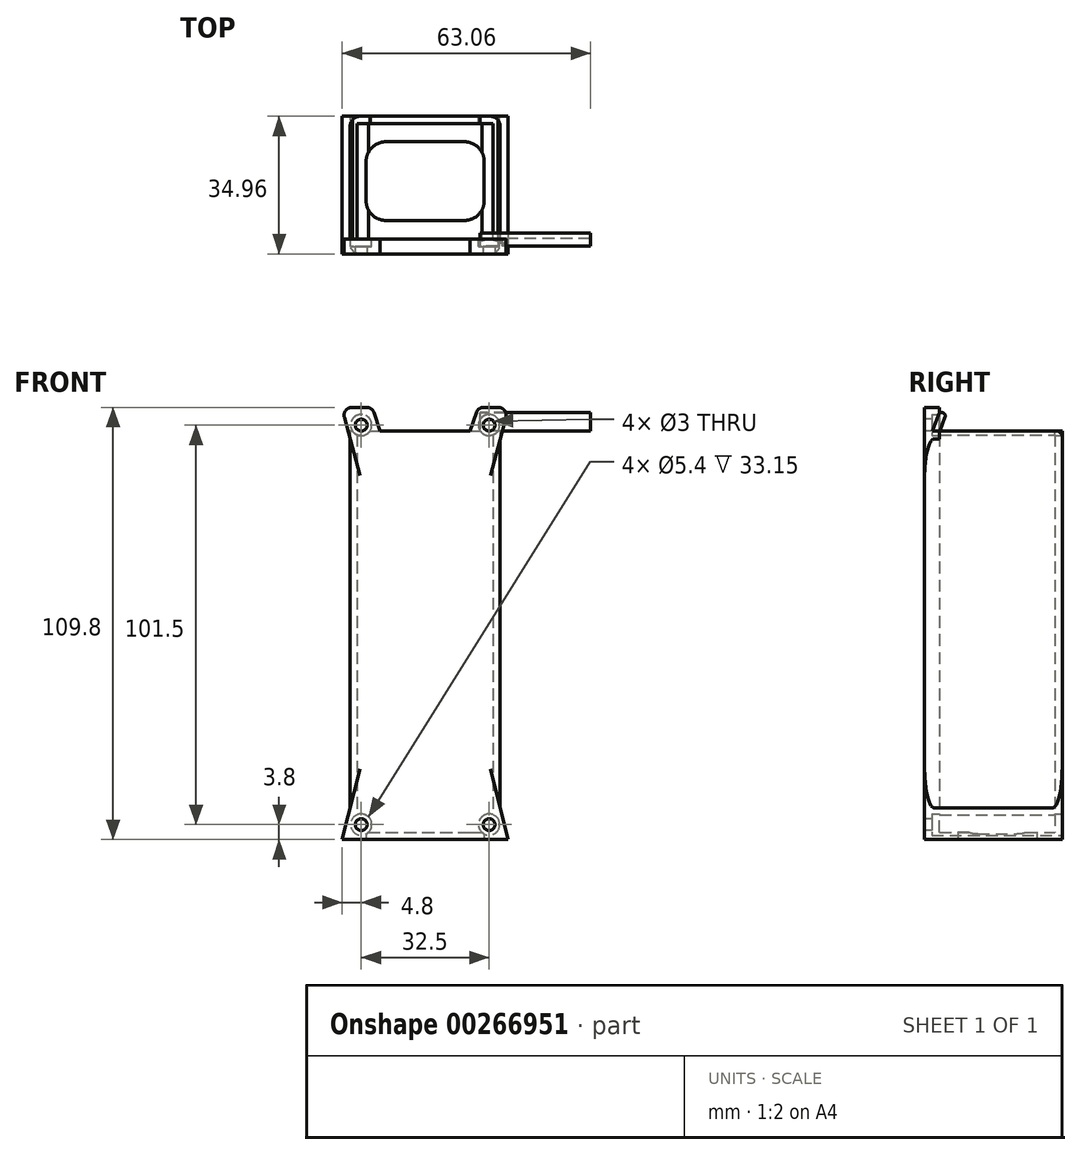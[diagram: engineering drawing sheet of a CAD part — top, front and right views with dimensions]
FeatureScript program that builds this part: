
annotation { "Feature Type Name" : "Feature", "Feature Type Description" : "" }
export const myFeature = defineFeature(function(context is Context, id is Id, definition is map)
    precondition{}
    {
        {
            assignVariable(context, id + "F0", {"name" : "battLength", "anyValue" : 102});
        }
        {
            assignVariable(context, id + "F1", {"name" : "defaultThickness", "anyValue" : 1.8});
        }
        {
            assignVariable(context, id + "F2", {"name" : "screwHeadDepth", "anyValue" : 2});
        }
        {
            var Q0;
            Q0=qCreatedBy(makeId("Top.planeOp"),FACE);
            var sketch = newSketch(context, id + "F3", { "sketchPlane" : qUnion([Q0])});
            skLineSegment(sketch, "E0.bottom", {"start": v(-17.25, 14.67) * mm, "end": v(17.25, 14.67) * mm});
            skLineSegment(sketch, "E0.top", {"start": v(-17.25, -14.68) * mm, "end": v(17.25, -14.68) * mm});
            skLineSegment(sketch, "E0.left", {"start": v(-17.25, 14.67) * mm, "end": v(-17.25, -14.68) * mm});
            skLineSegment(sketch, "E0.right", {"start": v(17.25, 14.67) * mm, "end": v(17.25, -14.68) * mm});
            skPoint(sketch, "E0.middle", {"position": v(0, 0) * mm});
            skLineSegment(sketch, "E1.0", {"start": v(-19.05, 16.47) * mm, "end": v(19.05, 16.47) * mm});
            skLineSegment(sketch, "E1.1", {"start": v(-19.05, 16.47) * mm, "end": v(-19.05, -16.48) * mm});
            skLineSegment(sketch, "E1.2", {"start": v(-19.05, -16.48) * mm, "end": v(19.05, -16.48) * mm});
            skLineSegment(sketch, "E1.3", {"start": v(19.05, 16.47) * mm, "end": v(19.05, -16.48) * mm});
            skSolve(sketch);
        }
        {
            var Q0;
            Q0 = qSketchRegion(id + "F3", true);
            extrude(context, id + "F4", {"entities" : qUnion([Q0]), "depth" : (getVariable(context, 'battLength')) * mm});
        }
        {
            var Q0;
            Q0=makeQuery(id+"F4.opExtrude","SWEPT_FACE",FACE,{"disambiguationData":[OSD([sQuery(id+"F3.wireOp",EDGE,"E1.2")])]});
            var sketch = newSketch(context, id + "F5", { "sketchPlane" : qUnion([Q0])});
            skCircle(sketch, "E2", {"center": v(-16.25, 2) * mm, "radius": 1.5 * mm});
            skCircle(sketch, "E3", {"center": v(-16.25, 103.5) * mm, "radius": 1.5 * mm});
            skCircle(sketch, "E4", {"center": v(16.25, 103.5) * mm, "radius": 1.5 * mm});
            skCircle(sketch, "E5", {"center": v(16.25, 2) * mm, "radius": 1.5 * mm});
            skSolve(sketch);
        }
        {
            var Q0;
            Q0=makeQuery(id+"F5.imprint","IMPRINT",FACE,{"disambiguationData":[TD([[makeQuery(id+"F5.imprint","IMPRINT",EDGE,{"derivedFrom":sQuery(id+"F5.wireOp",EDGE,"E2")}),-1.0]])]});
            var sketch = newSketch(context, id + "F6", { "sketchPlane" : qUnion([Q0])});
            skLineSegment(sketch, "E6", {"start": v(-19.05, 102) * mm, "end": v(-19.05, 108) * mm});
            skLineSegment(sketch, "E7", {"start": v(-19.05, 108) * mm, "end": v(-13.45, 108) * mm});
            skLineSegment(sketch, "E8", {"start": v(-13.45, 108) * mm, "end": v(-13.45, 102) * mm});
            skLineSegment(sketch, "E9.MirrorCS", {"start": v(13.45, 108) * mm, "end": v(13.45, 102) * mm});
            skLineSegment(sketch, "E10.MirrorCS", {"start": v(19.05, 108) * mm, "end": v(13.45, 108) * mm});
            skLineSegment(sketch, "E11.MirrorCS", {"start": v(19.05, 102) * mm, "end": v(19.05, 108) * mm});
            skLineSegment(sketch, "E12", {"start": v(-19.05, 102) * mm, "end": v(-13.45, 102) * mm});
            skLineSegment(sketch, "E13", {"start": v(13.45, 102) * mm, "end": v(19.05, 102) * mm});
            skSolve(sketch);
        }
        {
            var Q0;
            Q0 = qSketchRegion(id + "F6", true);
            extrude(context, id + "F7", {"entities" : qUnion([Q0]), "oppositeDirection" : true, "depth" : (getVariable(context, 'defaultThickness')) * mm});
        }
        {
            var Q0;
            Q0=makeQuery(id+"F4.opExtrude","SWEPT_BODY",BODY,{"disambiguationData":[OSD([sQuery(id+"F3.wireOp",EDGE,"E0.bottom"),sQuery(id+"F3.wireOp",EDGE,"E0.top"),sQuery(id+"F3.wireOp",EDGE,"E0.left"),sQuery(id+"F3.wireOp",EDGE,"E0.right"),sQuery(id+"F3.wireOp",EDGE,"E1.0"),sQuery(id+"F3.wireOp",EDGE,"E1.1"),sQuery(id+"F3.wireOp",EDGE,"E1.2"),sQuery(id+"F3.wireOp",EDGE,"E1.3")])]});
            var Q1;
            Q1=makeQuery(id+"F7.opExtrude","SWEPT_BODY",BODY,{"disambiguationData":[OSD([sQuery(id+"F6.wireOp",EDGE,"E6"),sQuery(id+"F6.wireOp",EDGE,"E7"),sQuery(id+"F6.wireOp",EDGE,"E8"),sQuery(id+"F6.wireOp",EDGE,"E12")])]});
            var Q2;
            Q2=makeQuery(id+"F7.opExtrude","SWEPT_BODY",BODY,{"disambiguationData":[OSD([sQuery(id+"F6.wireOp",EDGE,"E9.MirrorCS"),sQuery(id+"F6.wireOp",EDGE,"E10.MirrorCS"),sQuery(id+"F6.wireOp",EDGE,"E11.MirrorCS"),sQuery(id+"F6.wireOp",EDGE,"E13")])]});
            booleanBodies(context, id + "F8", {"operationType" : BooleanOperationType.UNION, "tools" : qUnion([Q0, Q1, Q2])});
        }
        {
            var Q0;
            Q0=makeQuery(id+"F5.imprint","IMPRINT",FACE,{"disambiguationData":[TD([[makeQuery(id+"F5.imprint","IMPRINT",EDGE,{"derivedFrom":sQuery(id+"F5.wireOp",EDGE,"E2")}),-1.0]])]});
            var Q1;
            Q1=makeQuery(id+"F8.opBoolean","MERGE",FACE,{"derivedFrom":[makeQuery(id+"F4.opExtrude","SWEPT_FACE",FACE,{"disambiguationData":[OSD([sQuery(id+"F3.wireOp",EDGE,"E1.2")])]}),makeQuery(id+"F7.opExtrude","CAP_FACE",FACE,{"disambiguationData":[OSD([sQuery(id+"F6.wireOp",EDGE,"E6"),sQuery(id+"F6.wireOp",EDGE,"E7"),sQuery(id+"F6.wireOp",EDGE,"E8"),sQuery(id+"F6.wireOp",EDGE,"E12")])],"isStart":true}),makeQuery(id+"F7.opExtrude","CAP_FACE",FACE,{"disambiguationData":[OSD([sQuery(id+"F6.wireOp",EDGE,"E9.MirrorCS"),sQuery(id+"F6.wireOp",EDGE,"E10.MirrorCS"),sQuery(id+"F6.wireOp",EDGE,"E11.MirrorCS"),sQuery(id+"F6.wireOp",EDGE,"E13")])],"isStart":true})]});
            extrude(context, id + "F9", {"entities" : qUnion([Q0, Q1]), "operationType" : NewBodyOperationType.ADD, "depth" : (getVariable(context, 'screwHeadDepth')) * mm});
        }
        {
            var Q0;
            Q0 = qSketchRegion(id + "F5", true);
            extrude(context, id + "F10", {"entities" : qUnion([Q0]), "operationType" : NewBodyOperationType.REMOVE, "endBound" : BoundingType.THROUGH_ALL, "oppositeDirection" : true, "depth" : 25 * mm, "hasSecondDirection" : true, "secondDirectionOppositeDirection" : false, "secondDirectionDepth" : 25 * mm});
        }
        {
            var Q0;
            {var subQ0=sQuery(id+"F3.wireOp",EDGE,"E1.2");Q0=makeQuery(id+"F9.boolean.opBoolean","MERGE",FACE,{"derivedFrom":[makeQuery(id+"F4.opExtrude","CAP_FACE",FACE,{"disambiguationData":[OSD([sQuery(id+"F3.wireOp",EDGE,"E0.bottom"),sQuery(id+"F3.wireOp",EDGE,"E0.top"),sQuery(id+"F3.wireOp",EDGE,"E0.left"),sQuery(id+"F3.wireOp",EDGE,"E0.right"),sQuery(id+"F3.wireOp",EDGE,"E1.0"),sQuery(id+"F3.wireOp",EDGE,"E1.1"),subQ0,sQuery(id+"F3.wireOp",EDGE,"E1.3")])],"isStart":true}),makeQuery(id+"F9.opExtrude","SWEPT_FACE",FACE,{"disambiguationData":[OSD([subQ0]),TDD([makeQuery(id+"F5.imprint","IMPRINT",EDGE,{"derivedFrom":makeQuery(id+"F4.opExtrude","CAP_EDGE",EDGE,{"disambiguationData":[OSD([subQ0])],"isStart":true})})])]})]});}
            var sketch = newSketch(context, id + "F11", { "sketchPlane" : qUnion([Q0])});
            skLineSegment(sketch, "E14.bottom", {"start": v(-19.05, 18.48) * mm, "end": v(19.05, 18.48) * mm});
            skLineSegment(sketch, "E14.top", {"start": v(-19.05, -16.47) * mm, "end": v(19.05, -16.47) * mm});
            skLineSegment(sketch, "E14.left", {"start": v(-19.05, 18.48) * mm, "end": v(-19.05, -16.47) * mm});
            skLineSegment(sketch, "E14.right", {"start": v(19.05, 18.48) * mm, "end": v(19.05, -16.47) * mm});
            skSolve(sketch);
        }
        {
            var Q0;
            Q0 = qSketchRegion(id + "F11", true);
            extrude(context, id + "F12", {"entities" : qUnion([Q0]), "operationType" : NewBodyOperationType.ADD, "depth" : (getVariable(context, 'defaultThickness')) * mm});
        }
        {
            var Q0;
            {var subQ0=sQuery(id+"F3.wireOp",EDGE,"E1.2");Q0=makeQuery(id+"F12.boolean.opBoolean","MERGE",FACE,{"derivedFrom":[makeQuery(id+"F9.boolean.opBoolean","MERGE",FACE,{"derivedFrom":[makeQuery(id+"F9.opExtrude","CAP_FACE",FACE,{"disambiguationData":[OSD([sQuery(id+"F3.wireOp",EDGE,"E1.1"),subQ0,sQuery(id+"F3.wireOp",EDGE,"E1.3"),sQuery(id+"F5.wireOp",EDGE,"E2"),sQuery(id+"F5.wireOp",EDGE,"E5")])],"isStart":false}),makeQuery(id+"F9.opExtrude","CAP_FACE",FACE,{"disambiguationData":[OSD([subQ0,sQuery(id+"F6.wireOp",EDGE,"E6"),sQuery(id+"F6.wireOp",EDGE,"E7"),sQuery(id+"F6.wireOp",EDGE,"E8"),sQuery(id+"F6.wireOp",EDGE,"E9.MirrorCS"),sQuery(id+"F6.wireOp",EDGE,"E10.MirrorCS"),sQuery(id+"F6.wireOp",EDGE,"E11.MirrorCS"),sQuery(id+"F6.wireOp",EDGE,"E12"),sQuery(id+"F6.wireOp",EDGE,"E13")])],"isStart":false})]}),makeQuery(id+"F12.opExtrude","SWEPT_FACE",FACE,{"disambiguationData":[OSD([sQuery(id+"F11.wireOp",EDGE,"E14.bottom")])]})]});}
            var sketch = newSketch(context, id + "F13", { "sketchPlane" : qUnion([Q0])});
            skLineSegment(sketch, "E15", {"start": v(-19.05, 108) * mm, "end": v(-21.2, 108) * mm});
            skLineSegment(sketch, "E16", {"start": v(-21.2, 108) * mm, "end": v(-19.05, 100) * mm});
            skLineSegment(sketch, "E17", {"start": v(-19.05, 100) * mm, "end": v(-19.05, 108) * mm});
            skLineSegment(sketch, "E18", {"start": v(-19.05, -1.8) * mm, "end": v(-21.05, -1.8) * mm});
            skLineSegment(sketch, "E19", {"start": v(-21.05, -1.8) * mm, "end": v(-19.05, 6.2) * mm});
            skLineSegment(sketch, "E20", {"start": v(-19.05, 6.2) * mm, "end": v(-19.05, -1.8) * mm});
            skLineSegment(sketch, "E21.MirrorCS", {"start": v(19.05, 6.2) * mm, "end": v(19.05, -1.8) * mm});
            skLineSegment(sketch, "E22.MirrorCS", {"start": v(21.05, -1.8) * mm, "end": v(19.05, 6.2) * mm});
            skLineSegment(sketch, "E23.MirrorCS", {"start": v(19.05, -1.8) * mm, "end": v(21.05, -1.8) * mm});
            skLineSegment(sketch, "E24.MirrorCS", {"start": v(19.05, 108) * mm, "end": v(21.2, 108) * mm});
            skLineSegment(sketch, "E25.MirrorCS", {"start": v(21.2, 108) * mm, "end": v(19.05, 100) * mm});
            skLineSegment(sketch, "E26.MirrorCS", {"start": v(19.05, 100) * mm, "end": v(19.05, 108) * mm});
            skLineSegment(sketch, "E27", {"start": v(13.45, 108) * mm, "end": v(11.45, 102) * mm});
            skLineSegment(sketch, "E28", {"start": v(11.45, 102) * mm, "end": v(13.45, 102) * mm});
            skLineSegment(sketch, "E29", {"start": v(13.45, 102) * mm, "end": v(13.45, 108) * mm});
            skLineSegment(sketch, "E30.MirrorCS", {"start": v(-11.45, 102) * mm, "end": v(-13.45, 102) * mm});
            skLineSegment(sketch, "E31.MirrorCS", {"start": v(-13.45, 108) * mm, "end": v(-11.45, 102) * mm});
            skLineSegment(sketch, "E32.MirrorCS", {"start": v(-13.45, 102) * mm, "end": v(-13.45, 108) * mm});
            skSolve(sketch);
        }
        {
            var Q0;
            Q0 = qSketchRegion(id + "F13", true);
            extrude(context, id + "F14", {"entities" : qUnion([Q0]), "operationType" : NewBodyOperationType.ADD, "oppositeDirection" : true, "depth" : (getVariable(context, 'screwHeadDepth') + getVariable(context, 'defaultThickness')) * mm});
        }
        {
            var Q0;
            Q0=makeQuery(id+"F8.opBoolean","MERGE",FACE,{"derivedFrom":[makeQuery(id+"F4.opExtrude","SWEPT_FACE",FACE,{"disambiguationData":[OSD([sQuery(id+"F3.wireOp",EDGE,"E0.top")])]}),makeQuery(id+"F7.opExtrude","CAP_FACE",FACE,{"disambiguationData":[OSD([sQuery(id+"F6.wireOp",EDGE,"E6"),sQuery(id+"F6.wireOp",EDGE,"E7"),sQuery(id+"F6.wireOp",EDGE,"E8"),sQuery(id+"F6.wireOp",EDGE,"E12")])],"isStart":false}),makeQuery(id+"F7.opExtrude","CAP_FACE",FACE,{"disambiguationData":[OSD([sQuery(id+"F6.wireOp",EDGE,"E9.MirrorCS"),sQuery(id+"F6.wireOp",EDGE,"E10.MirrorCS"),sQuery(id+"F6.wireOp",EDGE,"E11.MirrorCS"),sQuery(id+"F6.wireOp",EDGE,"E13")])],"isStart":false})]});
            var sketch = newSketch(context, id + "F15", { "sketchPlane" : qUnion([Q0])});
            skCircle(sketch, "E33", {"center": v(-16.25, 103.5) * mm, "radius": 2.7 * mm});
            skCircle(sketch, "E34", {"center": v(16.25, 103.5) * mm, "radius": 2.7 * mm});
            skCircle(sketch, "E35", {"center": v(-16.25, 2) * mm, "radius": 2.7 * mm});
            skCircle(sketch, "E36", {"center": v(16.25, 2) * mm, "radius": 2.7 * mm});
            skSolve(sketch);
        }
        {
            var Q0;
            Q0 = qSketchRegion(id + "F15", true);
            extrude(context, id + "F16", {"entities" : qUnion([Q0]), "operationType" : NewBodyOperationType.REMOVE, "oppositeDirection" : true, "depth" : (getVariable(context, 'screwHeadDepth')) * mm, "hasSecondDirection" : true, "secondDirectionBound" : SecondDirectionBoundingType.THROUGH_ALL, "secondDirectionOppositeDirection" : false, "secondDirectionDepth" : 25 * mm});
        }
        {
            var Q0;
            Q0=makeQuery(id+"F14.opExtrude","CAP_FACE",FACE,{"disambiguationData":[OSD([sQuery(id+"F13.wireOp",EDGE,"E18"),sQuery(id+"F13.wireOp",EDGE,"E19"),sQuery(id+"F13.wireOp",EDGE,"E20")])],"isStart":false});
            var Q1;
            Q1=makeQuery(id+"F14.opExtrude","CAP_FACE",FACE,{"disambiguationData":[OSD([sQuery(id+"F13.wireOp",EDGE,"E21.MirrorCS"),sQuery(id+"F13.wireOp",EDGE,"E22.MirrorCS"),sQuery(id+"F13.wireOp",EDGE,"E23.MirrorCS")])],"isStart":false});
            var Q2;
            Q2=makeQuery(id+"F12.boolean.opBoolean","MERGE",FACE,{"derivedFrom":[makeQuery(id+"F4.opExtrude","SWEPT_FACE",FACE,{"disambiguationData":[OSD([sQuery(id+"F3.wireOp",EDGE,"E1.0")])]}),makeQuery(id+"F12.opExtrude","SWEPT_FACE",FACE,{"disambiguationData":[OSD([sQuery(id+"F11.wireOp",EDGE,"E14.top")])]})]});
            extrude(context, id + "F17", {"entities" : qUnion([Q0, Q1]), "operationType" : NewBodyOperationType.ADD, "endBound" : BoundingType.UP_TO_SURFACE, "endBoundEntityFace" : qUnion([Q2]), "depth" : 25 * mm});
        }
        {
            var Q0;
            {var subQ0=sQuery(id+"F13.wireOp",EDGE,"E23.MirrorCS");var subQ1=sQuery(id+"F13.wireOp",EDGE,"E18");Q0=makeQuery(id+"F17.boolean.opBoolean","MERGE",FACE,{"derivedFrom":[makeQuery(id+"F14.boolean.opBoolean","MERGE",FACE,{"derivedFrom":[makeQuery(id+"F12.opExtrude","CAP_FACE",FACE,{"disambiguationData":[OSD([sQuery(id+"F11.wireOp",EDGE,"E14.bottom"),sQuery(id+"F11.wireOp",EDGE,"E14.top"),sQuery(id+"F11.wireOp",EDGE,"E14.left"),sQuery(id+"F11.wireOp",EDGE,"E14.right")])],"isStart":false}),makeQuery(id+"F14.opExtrude","SWEPT_FACE",FACE,{"disambiguationData":[OSD([subQ1])]}),makeQuery(id+"F14.opExtrude","SWEPT_FACE",FACE,{"disambiguationData":[OSD([subQ0])]})]}),makeQuery(id+"F17.opExtrude","SWEPT_FACE",FACE,{"disambiguationData":[OSD([subQ1])]}),makeQuery(id+"F17.opExtrude","SWEPT_FACE",FACE,{"disambiguationData":[OSD([subQ0])]})]});}
            var sketch = newSketch(context, id + "F18", { "sketchPlane" : qUnion([Q0])});
            skLineSegment(sketch, "E37", {"start": v(0, 18.48) * mm, "end": v(0, -16.47) * mm});
            skLineSegment(sketch, "E38", {"start": v(0, 0) * mm, "end": v(-21.05, 0) * mm});
            skLineSegment(sketch, "E39", {"start": v(-21.05, 0) * mm, "end": v(0, 0) * mm});
            skLineSegment(sketch, "E40", {"start": v(21.05, 0) * mm, "end": v(0, 0) * mm});
            skLineSegment(sketch, "E41.bottom", {"start": v(-10, 10) * mm, "end": v(10, 10) * mm});
            skLineSegment(sketch, "E41.top", {"start": v(-10, -10) * mm, "end": v(10, -10) * mm});
            skLineSegment(sketch, "E41.left", {"start": v(-15, 5) * mm, "end": v(-15, -5) * mm});
            skLineSegment(sketch, "E41.right", {"start": v(15, 5) * mm, "end": v(15, -5) * mm});
            skPoint(sketch, "E41.middle", {"position": v(0, 0) * mm});
            skPoint(sketch, "E42.visualSharp", {"position": v(-15, 10) * mm});
            skArc(sketch, "E42.filletArc", {"start": v(-10, 10) * mm, "mid": v(-13.54, 8.53) * mm, "end": v(-15, 5) * mm});
            skPoint(sketch, "E43.visualSharp", {"position": v(-15, -10) * mm});
            skArc(sketch, "E43.filletArc", {"start": v(-15, -5) * mm, "mid": v(-13.54, -8.53) * mm, "end": v(-10, -10) * mm});
            skPoint(sketch, "E44.visualSharp", {"position": v(15, -10) * mm});
            skArc(sketch, "E44.filletArc", {"start": v(10, -10) * mm, "mid": v(13.54, -8.53) * mm, "end": v(15, -5) * mm});
            skPoint(sketch, "E45.visualSharp", {"position": v(15, 10) * mm});
            skArc(sketch, "E45.filletArc", {"start": v(15, 5) * mm, "mid": v(13.54, 8.53) * mm, "end": v(10, 10) * mm});
            skSolve(sketch);
        }
        {
            var Q0;
            Q0 = qSketchRegion(id + "F18", true);
            extrude(context, id + "F19", {"entities" : qUnion([Q0]), "operationType" : NewBodyOperationType.REMOVE, "oppositeDirection" : true, "depth" : 25 * mm});
        }
        {
            var Q0;
            Q0=makeQuery(id+"F12.boolean.opBoolean","MERGE",EDGE,{"derivedFrom":[makeQuery(id+"F4.opExtrude","SWEPT_EDGE",EDGE,{"disambiguationData":[OSD([sQuery(id+"F3.wireOp",EDGE,"E1.0"),sQuery(id+"F3.wireOp",EDGE,"E1.1")])]}),makeQuery(id+"F12.opExtrude","SWEPT_EDGE",EDGE,{"disambiguationData":[OSD([sQuery(id+"F11.wireOp",EDGE,"E14.top"),sQuery(id+"F11.wireOp",EDGE,"E14.left")])]})]});
            var Q1;
            Q1=makeQuery(id+"F12.boolean.opBoolean","MERGE",EDGE,{"derivedFrom":[makeQuery(id+"F4.opExtrude","SWEPT_EDGE",EDGE,{"disambiguationData":[OSD([sQuery(id+"F3.wireOp",EDGE,"E1.0"),sQuery(id+"F3.wireOp",EDGE,"E1.3")])]}),makeQuery(id+"F12.opExtrude","SWEPT_EDGE",EDGE,{"disambiguationData":[OSD([sQuery(id+"F11.wireOp",EDGE,"E14.top"),sQuery(id+"F11.wireOp",EDGE,"E14.right")])]})]});
            var Q2;
            {var subQ0=sQuery(id+"F3.wireOp",EDGE,"E1.3");var subQ1=sQuery(id+"F3.wireOp",EDGE,"E1.2");Q2=makeQuery(id+"F12.boolean.opBoolean","MERGE",EDGE,{"derivedFrom":[makeQuery(id+"F9.boolean.opBoolean","MERGE",EDGE,{"derivedFrom":[makeQuery(id+"F9.opExtrude","CAP_EDGE",EDGE,{"disambiguationData":[OSD([subQ1,subQ0])],"isStart":false}),makeQuery(id+"F9.opExtrude","CAP_EDGE",EDGE,{"disambiguationData":[OSD([subQ1,subQ0,sQuery(id+"F6.wireOp",EDGE,"E11.MirrorCS")])],"isStart":false})]}),makeQuery(id+"F12.opExtrude","SWEPT_EDGE",EDGE,{"disambiguationData":[OSD([sQuery(id+"F11.wireOp",EDGE,"E14.bottom"),sQuery(id+"F11.wireOp",EDGE,"E14.right")])]})]});}
            var Q3;
            {var subQ0=sQuery(id+"F3.wireOp",EDGE,"E1.2");var subQ1=sQuery(id+"F3.wireOp",EDGE,"E1.1");Q3=makeQuery(id+"F12.boolean.opBoolean","MERGE",EDGE,{"derivedFrom":[makeQuery(id+"F9.boolean.opBoolean","MERGE",EDGE,{"derivedFrom":[makeQuery(id+"F9.opExtrude","CAP_EDGE",EDGE,{"disambiguationData":[OSD([subQ1,subQ0])],"isStart":false}),makeQuery(id+"F9.opExtrude","CAP_EDGE",EDGE,{"disambiguationData":[OSD([subQ1,subQ0,sQuery(id+"F6.wireOp",EDGE,"E6")])],"isStart":false})]}),makeQuery(id+"F12.opExtrude","SWEPT_EDGE",EDGE,{"disambiguationData":[OSD([sQuery(id+"F11.wireOp",EDGE,"E14.bottom"),sQuery(id+"F11.wireOp",EDGE,"E14.left")])]})]});}
            fillet(context, id + "F20", {"entities" : qUnion([Q0, Q1, Q2, Q3]), "radius" : 2.5 * mm, "tangentPropagation" : true, "allowEdgeOverflow" : false});
        }
        {
            var Q0;
            {var subQ0=sQuery(id+"F6.wireOp",EDGE,"E7");var subQ1=sQuery(id+"F6.wireOp",EDGE,"E8");Q0=makeQuery(id+"F14.boolean.opBoolean","MERGE",EDGE,{"derivedFrom":[makeQuery(id+"F9.boolean.opBoolean","MERGE",EDGE,{"derivedFrom":[makeQuery(id+"F7.opExtrude","SWEPT_EDGE",EDGE,{"disambiguationData":[OSD([subQ0,subQ1])]}),makeQuery(id+"F9.opExtrude","SWEPT_EDGE",EDGE,{"disambiguationData":[OSD([subQ0,subQ1])]})]}),makeQuery(id+"F14.opExtrude","SWEPT_EDGE",EDGE,{"disambiguationData":[OSD([subQ0,sQuery(id+"F13.wireOp",EDGE,"E31.MirrorCS"),sQuery(id+"F13.wireOp",EDGE,"E32.MirrorCS")])]})]});}
            var Q1;
            Q1=makeQuery(id+"F14.opExtrude","SWEPT_EDGE",EDGE,{"disambiguationData":[OSD([sQuery(id+"F13.wireOp",EDGE,"E15"),sQuery(id+"F13.wireOp",EDGE,"E16")])]});
            var Q2;
            {var subQ0=sQuery(id+"F6.wireOp",EDGE,"E10.MirrorCS");var subQ1=sQuery(id+"F6.wireOp",EDGE,"E9.MirrorCS");Q2=makeQuery(id+"F14.boolean.opBoolean","MERGE",EDGE,{"derivedFrom":[makeQuery(id+"F9.boolean.opBoolean","MERGE",EDGE,{"derivedFrom":[makeQuery(id+"F7.opExtrude","SWEPT_EDGE",EDGE,{"disambiguationData":[OSD([subQ1,subQ0])]}),makeQuery(id+"F9.opExtrude","SWEPT_EDGE",EDGE,{"disambiguationData":[OSD([subQ1,subQ0])]})]}),makeQuery(id+"F14.opExtrude","SWEPT_EDGE",EDGE,{"disambiguationData":[OSD([subQ0,sQuery(id+"F13.wireOp",EDGE,"E27"),sQuery(id+"F13.wireOp",EDGE,"E29")])]})]});}
            var Q3;
            Q3=makeQuery(id+"F14.opExtrude","SWEPT_EDGE",EDGE,{"disambiguationData":[OSD([sQuery(id+"F13.wireOp",EDGE,"E24.MirrorCS"),sQuery(id+"F13.wireOp",EDGE,"E25.MirrorCS")])]});
            fillet(context, id + "F21", {"entities" : qUnion([Q0, Q1, Q2, Q3]), "radius" : 2 * mm, "tangentPropagation" : true, "allowEdgeOverflow" : false});
        }
        {
            var Q0;
            {var subQ0=sQuery(id+"F3.wireOp",EDGE,"E1.3");var subQ1=sQuery(id+"F3.wireOp",EDGE,"E1.1");var subQ3=sQuery(id+"F3.wireOp",EDGE,"E1.0");var subQ4=sQuery(id+"F3.wireOp",EDGE,"E0.bottom");var subQ5=sQuery(id+"F3.wireOp",EDGE,"E0.top");var subQ7=sQuery(id+"F3.wireOp",EDGE,"E0.right");var subQ8=sQuery(id+"F3.wireOp",EDGE,"E0.left");Q0=makeQuery(id+"F16.boolean.opBoolean","INTERSECT",EDGE,{"disambiguationData":[OD(1.0)],"derivedFrom":[makeQuery(id+"F8.opBoolean","SPLIT",FACE,{"disambiguationData":[TD([makeQuery(id+"F4.opExtrude","SWEPT_FACE",FACE,{"disambiguationData":[OSD([subQ4])]})])],"derivedFrom":makeQuery(id+"F4.opExtrude","CAP_FACE",FACE,{"disambiguationData":[OSD([subQ4,subQ5,subQ8,subQ7,subQ3,subQ1,sQuery(id+"F3.wireOp",EDGE,"E1.2"),subQ0])],"isStart":false})}),makeQuery(id+"F16.opExtrude","SWEPT_FACE",FACE,{"disambiguationData":[OSD([sQuery(id+"F15.wireOp",EDGE,"E33")])]})]});}
            cPlane(context, id + "F22", {"entities" : qUnion([Q0]), "cplaneType" : CPlaneType.LINE_ANGLE, "offset" : 25 * mm, "angle" : 90 * degree, "width" : 150 * mm, "height" : 150 * mm});
        }
        {
            var Q0;
            Q0=qCreatedBy(id+"F22.planeOp",FACE);
            var sketch = newSketch(context, id + "F23", { "sketchPlane" : qUnion([Q0])});
            skLineSegment(sketch, "E46", {"start": v(16.48, 102) * mm, "end": v(14.76, 106.7) * mm});
            skLineSegment(sketch, "E47", {"start": v(14.76, 106.7) * mm, "end": v(12.85, 106.7) * mm});
            skLineSegment(sketch, "E48", {"start": v(12.85, 106.7) * mm, "end": v(14.57, 101.97) * mm});
            skLineSegment(sketch, "E49", {"start": v(14.57, 101.97) * mm, "end": v(16.47, 102) * mm});
            skSolve(sketch);
        }
        {
            var Q0;
            Q0=makeQuery(id+"F23.imprint","IMPRINT",FACE,{"disambiguationData":[TD([[makeQuery(id+"F23.imprint","IMPRINT",EDGE,{"derivedFrom":sQuery(id+"F23.wireOp",EDGE,"E46")}),1.0]])]});
            extrude(context, id + "F24", {"entities" : qUnion([Q0]), "operationType" : NewBodyOperationType.ADD, "oppositeDirection" : true, "depth" : 28 * mm});
        }
        {
            var Q0;
            Q0=makeQuery(id+"F24.opExtrude","SWEPT_EDGE",EDGE,{"disambiguationData":[OSD([sQuery(id+"F23.wireOp",EDGE,"E46"),sQuery(id+"F23.wireOp",EDGE,"E47")])]});
            var Q1;
            Q1=makeQuery(id+"F24.opExtrude","SWEPT_EDGE",EDGE,{"disambiguationData":[OSD([sQuery(id+"F23.wireOp",EDGE,"E47"),sQuery(id+"F23.wireOp",EDGE,"E48")])]});
            fillet(context, id + "F25", {"entities" : qUnion([Q0, Q1]), "radius" : (getVariable(context, 'defaultThickness') / 2) * mm, "tangentPropagation" : true, "allowEdgeOverflow" : false});
        }
    });
